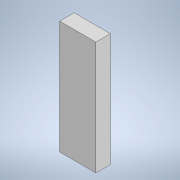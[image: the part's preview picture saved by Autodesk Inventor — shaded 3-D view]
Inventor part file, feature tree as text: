
AUTODESK INVENTOR PART (.ipt)
format: ipt  version: 2021.2 (Build 252289000, 289)  size: 114,688 bytes
history: native  units: in
note: dims shown in document units (in); Inventor stores cm internally (conversion verified against a paired STEP export)
features: extrude x3, sketch x3
ambient origin geometry x8: Origin, YZ Plane, XZ Plane, XY Plane, X Axis, Y Axis, Z Axis, Center Point
bodies: Solid1 (feature_tree)
feature tree (6):
  extrude  "Extrusion1"  Depth=3.0in
  extrude  "Extrusion3"  Depth=0.4in TaperAngle=0.0deg
  extrude  "Extrusion4"  Depth=0.275in
  sketch  "Sketch1"  dims[d0=1.0in d1=3.0in]
  sketch  "Sketch3"  dims[d2=0.4in d3=0.0in d6=0.13in d7=0.0in]
  sketch  "Sketch4"  dims[d9=0.15in d10=0.38in d11=0.275in d12=0.0in d13=0.0344in d14=0.0344in]
